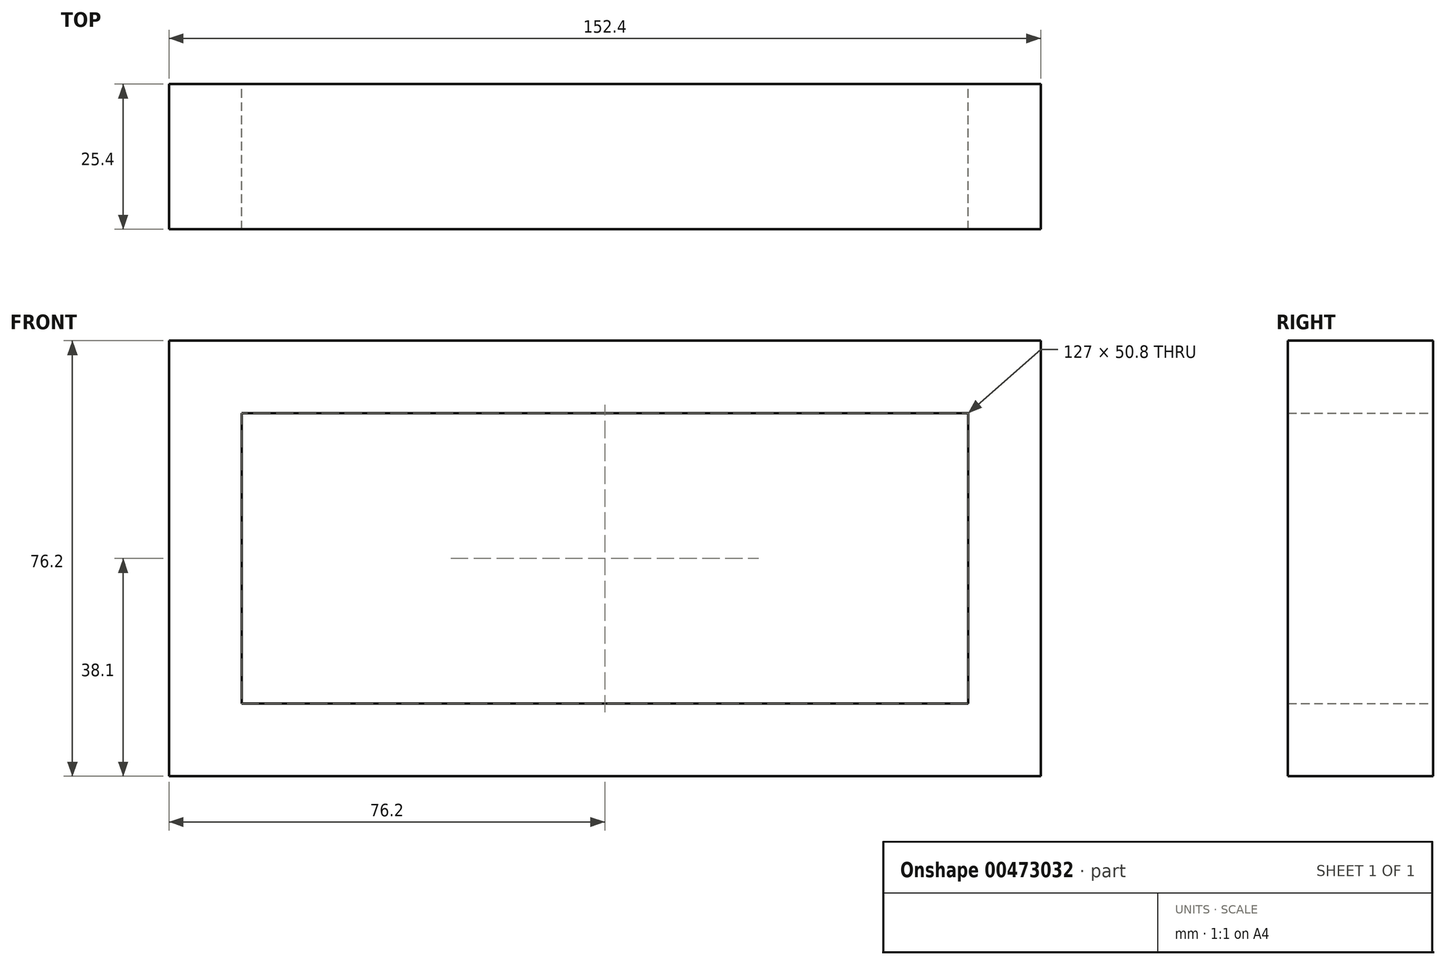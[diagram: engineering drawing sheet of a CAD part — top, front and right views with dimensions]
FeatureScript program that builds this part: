
annotation { "Feature Type Name" : "Feature", "Feature Type Description" : "" }
export const myFeature = defineFeature(function(context is Context, id is Id, definition is map)
    precondition{}
    {
        {
            var Q0;
            Q0=qCreatedBy(makeId("Front.planeOp"),FACE);
            var sketch = newSketch(context, id + "F0", { "sketchPlane" : qUnion([Q0])});
            skLineSegment(sketch, "E0.bottom", {"start": v(76.2, 38.1) * mm, "end": v(-76.2, 38.1) * mm});
            skLineSegment(sketch, "E0.top", {"start": v(76.2, -38.1) * mm, "end": v(-76.2, -38.1) * mm});
            skLineSegment(sketch, "E0.left", {"start": v(76.2, 38.1) * mm, "end": v(76.2, -38.1) * mm});
            skLineSegment(sketch, "E0.right", {"start": v(-76.2, 38.1) * mm, "end": v(-76.2, -38.1) * mm});
            skPoint(sketch, "E0.middle", {"position": v(0, 0) * mm});
            skLineSegment(sketch, "E1.bottom", {"start": v(63.5, 25.4) * mm, "end": v(-63.5, 25.4) * mm});
            skLineSegment(sketch, "E1.top", {"start": v(63.5, -25.4) * mm, "end": v(-63.5, -25.4) * mm});
            skLineSegment(sketch, "E1.left", {"start": v(63.5, 25.4) * mm, "end": v(63.5, -25.4) * mm});
            skLineSegment(sketch, "E1.right", {"start": v(-63.5, 25.4) * mm, "end": v(-63.5, -25.4) * mm});
            skSolve(sketch);
        }
        {
            var Q0;
            Q0 = qSketchRegion(id + "F0", true);
            extrude(context, id + "F1", {"entities" : qUnion([Q0]), "depth" : 25.4 * mm});
        }
    });
